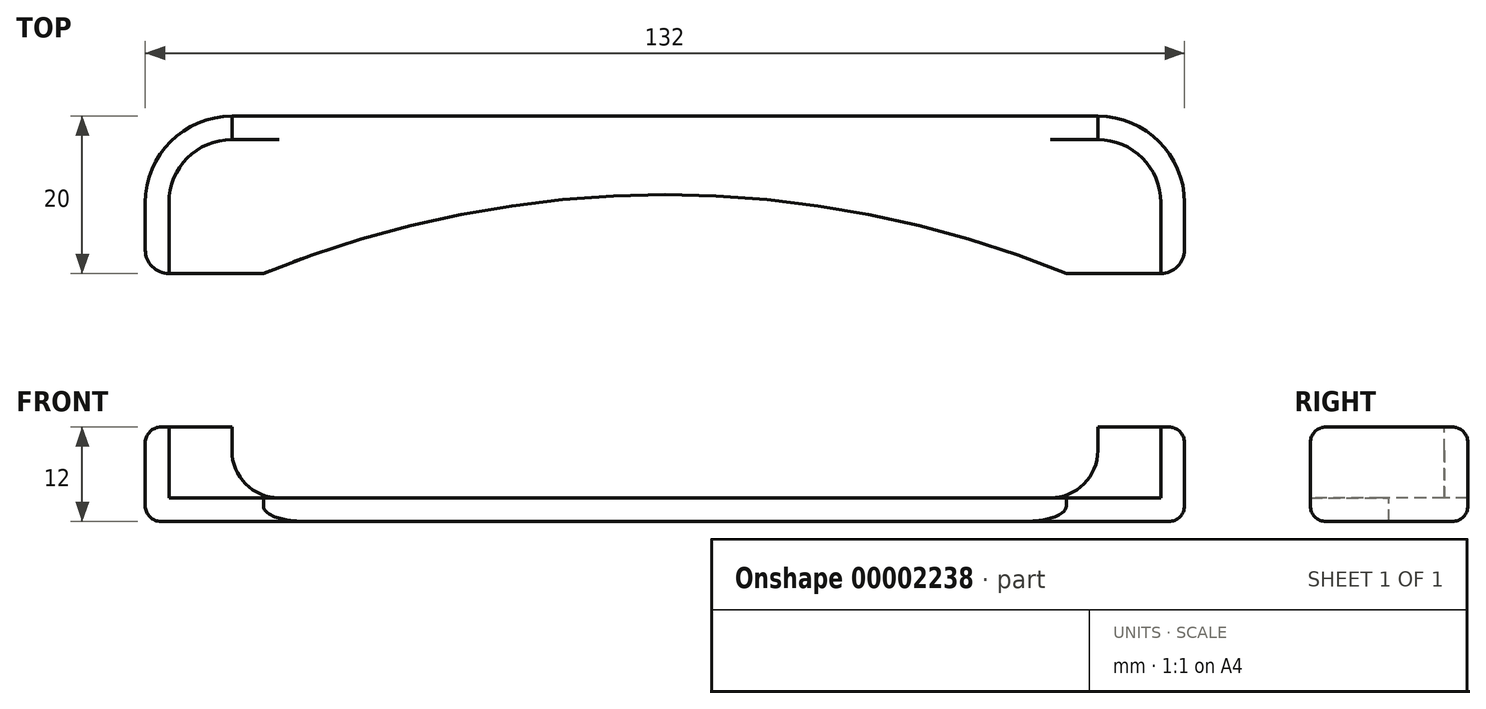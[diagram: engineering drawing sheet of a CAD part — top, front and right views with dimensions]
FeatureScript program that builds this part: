
annotation { "Feature Type Name" : "Feature", "Feature Type Description" : "" }
export const myFeature = defineFeature(function(context is Context, id is Id, definition is map)
    precondition{}
    {
        {
            var Q0;
            Q0=qCreatedBy(makeId("Top.planeOp"),FACE);
            var sketch = newSketch(context, id + "F0", { "sketchPlane" : qUnion([Q0])});
            skLineSegment(sketch, "E0.bottom", {"start": v(-55, 35) * mm, "end": v(55, 35) * mm});
            skLineSegment(sketch, "E0.top", {"start": v(-63, 15) * mm, "end": v(63, 15) * mm});
            skLineSegment(sketch, "E0.left", {"start": v(-66, 24) * mm, "end": v(-66, 18) * mm});
            skLineSegment(sketch, "E0.right", {"start": v(66, 24) * mm, "end": v(66, 18) * mm});
            skPoint(sketch, "E1.visualSharp", {"position": v(-66, 35) * mm});
            skArc(sketch, "E1.filletArc", {"start": v(-55, 35) * mm, "mid": v(-62.78, 31.78) * mm, "end": v(-66, 24) * mm});
            skPoint(sketch, "E2.visualSharp", {"position": v(66, 35) * mm});
            skArc(sketch, "E2.filletArc", {"start": v(66, 24) * mm, "mid": v(62.78, 31.78) * mm, "end": v(55, 35) * mm});
            skPoint(sketch, "E3.visualSharp", {"position": v(-66, 15) * mm});
            skArc(sketch, "E3.filletArc", {"start": v(-66, 18) * mm, "mid": v(-65.12, 15.88) * mm, "end": v(-63, 15) * mm});
            skPoint(sketch, "E4.visualSharp", {"position": v(66, 15) * mm});
            skArc(sketch, "E4.filletArc", {"start": v(63, 15) * mm, "mid": v(65.12, 15.88) * mm, "end": v(66, 18) * mm});
            skPoint(sketch, "E5", {"position": v(0, 15) * mm});
            skSolve(sketch);
        }
        {
            var Q0;
            Q0=makeQuery(id+"F0.imprint","IMPRINT",FACE,{"disambiguationData":[TD([[makeQuery(id+"F0.imprint","IMPRINT",EDGE,{"derivedFrom":sQuery(id+"F0.wireOp",EDGE,"E0.bottom")}),-1.0]])]});
            extrude(context, id + "F1", {"entities" : qUnion([Q0]), "depth" : 12 * mm});
        }
        {
            var Q0;
            Q0=makeQuery(id+"F1.opExtrude","CAP_FACE",FACE,{"disambiguationData":[OSD([sQuery(id+"F0.wireOp",EDGE,"E0.bottom"),sQuery(id+"F0.wireOp",EDGE,"E0.top"),sQuery(id+"F0.wireOp",EDGE,"E0.left"),sQuery(id+"F0.wireOp",EDGE,"E0.right"),sQuery(id+"F0.wireOp",EDGE,"E1.filletArc"),sQuery(id+"F0.wireOp",EDGE,"E2.filletArc"),sQuery(id+"F0.wireOp",EDGE,"E3.filletArc"),sQuery(id+"F0.wireOp",EDGE,"E4.filletArc")])],"isStart":false});
            var sketch = newSketch(context, id + "F2", { "sketchPlane" : qUnion([Q0])});
            skArc(sketch, "E6.1", {"start": v(63, 24) * mm, "mid": v(60.66, 29.66) * mm, "end": v(55, 32) * mm});
            skLineSegment(sketch, "E6.2", {"start": v(-55, 32) * mm, "end": v(55, 32) * mm});
            skArc(sketch, "E6.3", {"start": v(-55, 32) * mm, "mid": v(-60.66, 29.66) * mm, "end": v(-63, 24) * mm});
            skLineSegment(sketch, "E7", {"start": v(-63, 24) * mm, "end": v(-63, 15) * mm});
            skLineSegment(sketch, "E8", {"start": v(-63, 15) * mm, "end": v(63, 15) * mm});
            skLineSegment(sketch, "E9", {"start": v(63, 15) * mm, "end": v(63, 24) * mm});
            skSolve(sketch);
        }
        {
            var Q0;
            Q0=makeQuery(id+"F1.opExtrude","CAP_FACE",FACE,{"disambiguationData":[OSD([sQuery(id+"F0.wireOp",EDGE,"E0.bottom"),sQuery(id+"F0.wireOp",EDGE,"E0.top"),sQuery(id+"F0.wireOp",EDGE,"E0.left"),sQuery(id+"F0.wireOp",EDGE,"E0.right"),sQuery(id+"F0.wireOp",EDGE,"E1.filletArc"),sQuery(id+"F0.wireOp",EDGE,"E2.filletArc"),sQuery(id+"F0.wireOp",EDGE,"E3.filletArc"),sQuery(id+"F0.wireOp",EDGE,"E4.filletArc")])],"isStart":false});
            var Q1;
            Q1=makeQuery(id+"F1.opExtrude","CAP_FACE",FACE,{"disambiguationData":[OSD([sQuery(id+"F0.wireOp",EDGE,"E0.bottom"),sQuery(id+"F0.wireOp",EDGE,"E0.top"),sQuery(id+"F0.wireOp",EDGE,"E0.left"),sQuery(id+"F0.wireOp",EDGE,"E0.right"),sQuery(id+"F0.wireOp",EDGE,"E1.filletArc"),sQuery(id+"F0.wireOp",EDGE,"E2.filletArc"),sQuery(id+"F0.wireOp",EDGE,"E3.filletArc"),sQuery(id+"F0.wireOp",EDGE,"E4.filletArc")])],"isStart":true});
            fillet(context, id + "F3", {"entities" : qUnion([Q0, Q1]), "radius" : 2 * mm, "allowEdgeOverflow" : false});
        }
        {
            var Q0;
            Q0=makeQuery(id+"F2.imprint","IMPRINT",FACE,{"disambiguationData":[TD([[makeQuery(id+"F2.imprint","IMPRINT",EDGE,{"derivedFrom":sQuery(id+"F2.wireOp",EDGE,"001a4620-0fa9-427e-a59e-a394cfe2f85a.bottom")}),-1.0]])]});
            var Q1;
            Q1=makeQuery(id+"F2.imprint","IMPRINT",FACE,{"disambiguationData":[TD([[makeQuery(id+"F2.imprint","IMPRINT",EDGE,{"derivedFrom":sQuery(id+"F2.wireOp",EDGE,"E6.1")}),1.0]])]});
            extrude(context, id + "F4", {"entities" : qUnion([Q0, Q1]), "operationType" : NewBodyOperationType.REMOVE, "oppositeDirection" : true, "depth" : 9 * mm});
        }
        {
            var Q0;
            Q0=makeQuery(id+"F4.boolean.opBoolean","COPY",FACE,{"derivedFrom":makeQuery(id+"F4.opExtrude","CAP_FACE",FACE,{"disambiguationData":[OSD([sQuery(id+"F2.wireOp",EDGE,"E6.1"),sQuery(id+"F2.wireOp",EDGE,"E6.2"),sQuery(id+"F2.wireOp",EDGE,"E6.3"),sQuery(id+"F2.wireOp",EDGE,"E7"),sQuery(id+"F2.wireOp",EDGE,"E8"),sQuery(id+"F2.wireOp",EDGE,"E9")])],"isStart":false})});
            var sketch = newSketch(context, id + "F5", { "sketchPlane" : qUnion([Q0])});
            skArc(sketch, "E10", {"start": v(51, 15) * mm, "mid": v(0, 25) * mm, "end": v(-51, 15) * mm});
            skLineSegment(sketch, "E11", {"start": v(-51, 15) * mm, "end": v(51, 15) * mm});
            skLineSegment(sketch, "E12", {"start": v(0, 15) * mm, "end": v(0, -110.05) * mm, "construction": true});
            skSolve(sketch);
        }
        {
            var Q0;
            Q0=makeQuery(id+"F5.imprint","IMPRINT",FACE,{"disambiguationData":[TD([[makeQuery(id+"F5.imprint","IMPRINT",EDGE,{"derivedFrom":sQuery(id+"F5.wireOp",EDGE,"E10")}),1.0]])]});
            extrude(context, id + "F6", {"entities" : qUnion([Q0]), "operationType" : NewBodyOperationType.REMOVE, "endBound" : BoundingType.THROUGH_ALL, "oppositeDirection" : true, "depth" : 25 * mm});
        }
        {
            var Q0;
            Q0=makeQuery(id+"F4.boolean.opBoolean","COPY",FACE,{"derivedFrom":makeQuery(id+"F4.opExtrude","SWEPT_FACE",FACE,{"disambiguationData":[OSD([sQuery(id+"F2.wireOp",EDGE,"E6.2")])]})});
            var sketch = newSketch(context, id + "F7", { "sketchPlane" : qUnion([Q0])});
            skLineSegment(sketch, "E13", {"start": v(-55, 12) * mm, "end": v(-55, 9) * mm});
            skArc(sketch, "E14", {"start": v(-55, 9) * mm, "mid": v(-53.24, 4.76) * mm, "end": v(-49, 3) * mm});
            skLineSegment(sketch, "E15", {"start": v(-49, 3) * mm, "end": v(0, 3) * mm});
            skLineSegment(sketch, "E16", {"start": v(0, 3) * mm, "end": v(0, 12) * mm, "construction": true});
            skLineSegment(sketch, "E17", {"start": v(0, 12) * mm, "end": v(-55, 12) * mm});
            skLineSegment(sketch, "E18.0.MirrorCS", {"start": v(0, 12) * mm, "end": v(55, 12) * mm});
            skLineSegment(sketch, "E19.0.MirrorCS", {"start": v(55, 12) * mm, "end": v(55, 9) * mm});
            skArc(sketch, "E20.0.MirrorCS", {"start": v(55, 9) * mm, "mid": v(53.24, 4.76) * mm, "end": v(49, 3) * mm});
            skLineSegment(sketch, "E21.0.MirrorCS", {"start": v(49, 3) * mm, "end": v(0, 3) * mm});
            skSolve(sketch);
        }
        {
            var Q0;
            Q0=makeQuery(id+"F7.imprint","IMPRINT",FACE,{"disambiguationData":[TD([[makeQuery(id+"F7.imprint","IMPRINT",EDGE,{"derivedFrom":sQuery(id+"F7.wireOp",EDGE,"E13")}),-1.0]])]});
            extrude(context, id + "F8", {"entities" : qUnion([Q0]), "operationType" : NewBodyOperationType.REMOVE, "endBound" : BoundingType.THROUGH_ALL, "oppositeDirection" : true, "depth" : 25 * mm});
        }
    });
